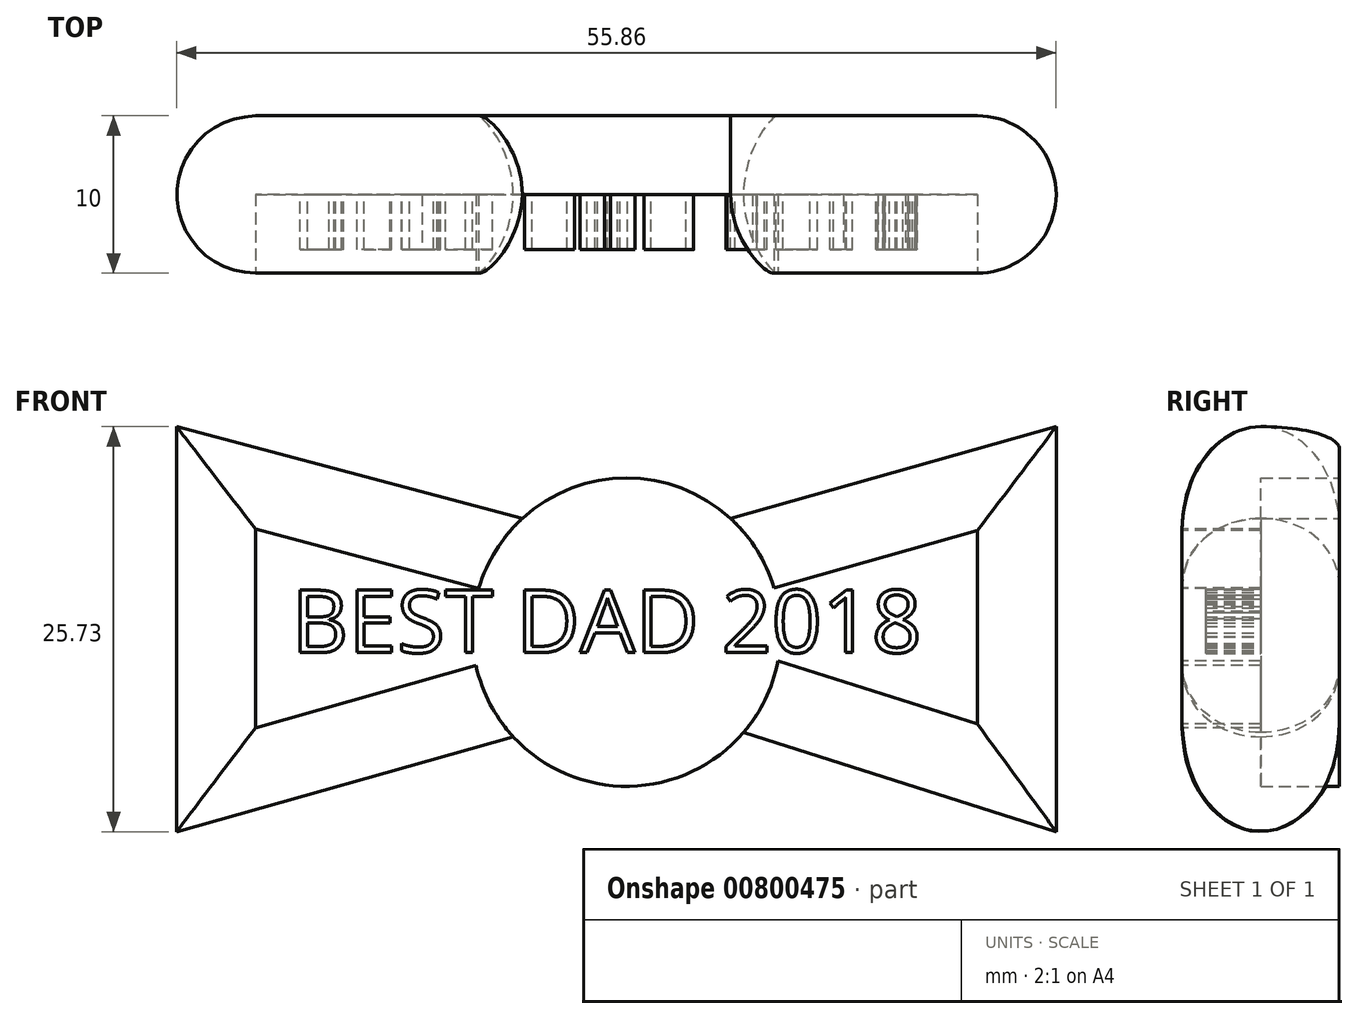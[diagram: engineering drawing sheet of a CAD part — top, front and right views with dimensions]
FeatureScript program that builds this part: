
annotation { "Feature Type Name" : "Feature", "Feature Type Description" : "" }
export const myFeature = defineFeature(function(context is Context, id is Id, definition is map)
    precondition{}
    {
        {
            var Q0;
            Q0=qCreatedBy(makeId("Front.planeOp"),FACE);
            var sketch = newSketch(context, id + "F0", { "sketchPlane" : qUnion([Q0])});
            skCircle(sketch, "E0", {"center": v(0, 0) * mm, "radius": 9.8 * mm});
            skLineSegment(sketch, "E1", {"start": v(6.62, 7.22) * mm, "end": v(27.3, 13.05) * mm});
            skLineSegment(sketch, "E2", {"start": v(27.3, 13.05) * mm, "end": v(27.3, -12.68) * mm});
            skLineSegment(sketch, "E3", {"start": v(27.3, -12.68) * mm, "end": v(7.43, -6.37) * mm});
            skLineSegment(sketch, "E4", {"start": v(7.43, -6.37) * mm, "end": v(6.62, 7.22) * mm});
            skLineSegment(sketch, "E5", {"start": v(-6.62, 7.22) * mm, "end": v(-28.57, 13.05) * mm});
            skLineSegment(sketch, "E6", {"start": v(-28.57, 13.05) * mm, "end": v(-28.57, -12.68) * mm});
            skLineSegment(sketch, "E7", {"start": v(-28.57, -12.68) * mm, "end": v(-7.2, -6.64) * mm});
            skLineSegment(sketch, "E8", {"start": v(-7.2, -6.64) * mm, "end": v(-6.62, 7.22) * mm});
            skSolve(sketch);
        }
        {
            var Q0;
            Q0 = qSketchRegion(id + "F0", true);
            extrude(context, id + "F1", {"entities" : qUnion([Q0]), "depth" : 10 * mm, "offsetDistance" : 25 * mm});
        }
        {
            var Q0;
            Q0=qCreatedBy(makeId("Front.planeOp"),FACE);
            var sketch = newSketch(context, id + "F2", { "sketchPlane" : qUnion([Q0])});
            skText(sketch, "E9", { "text": "BEST DAD 2018", "fontName": "OpenSans-Regular.ttf"});
            const initialGuessF2  = {"E9": [-0.02127, -0.0013, 1, 0, 0.004]};
            skSetInitialGuess(sketch, initialGuessF2);
            skSolve(sketch);
        }
        {
            var Q0;
            Q0=makeQuery(id+"F1.opExtrude","CAP_EDGE",EDGE,{"disambiguationData":[OSD([sQuery(id+"F0.wireOp",EDGE,"E5")])],"isStart":false});
            var Q1;
            Q1=makeQuery(id+"F1.opExtrude","CAP_EDGE",EDGE,{"disambiguationData":[OSD([sQuery(id+"F0.wireOp",EDGE,"E6")])],"isStart":false});
            var Q2;
            Q2=makeQuery(id+"F1.opExtrude","CAP_EDGE",EDGE,{"disambiguationData":[OSD([sQuery(id+"F0.wireOp",EDGE,"E7")])],"isStart":false});
            var Q3;
            Q3=makeQuery(id+"F1.opExtrude","CAP_EDGE",EDGE,{"disambiguationData":[OSD([sQuery(id+"F0.wireOp",EDGE,"E3")])],"isStart":false});
            var Q4;
            Q4=makeQuery(id+"F1.opExtrude","CAP_EDGE",EDGE,{"disambiguationData":[OSD([sQuery(id+"F0.wireOp",EDGE,"E2")])],"isStart":false});
            var Q5;
            Q5=makeQuery(id+"F1.opExtrude","CAP_EDGE",EDGE,{"disambiguationData":[OSD([sQuery(id+"F0.wireOp",EDGE,"E1")])],"isStart":false});
            var Q6;
            Q6=makeQuery(id+"F1.opExtrude","CAP_EDGE",EDGE,{"disambiguationData":[OSD([sQuery(id+"F0.wireOp",EDGE,"E5")])],"isStart":true});
            var Q7;
            Q7=makeQuery(id+"F1.opExtrude","CAP_EDGE",EDGE,{"disambiguationData":[OSD([sQuery(id+"F0.wireOp",EDGE,"E6")])],"isStart":true});
            var Q8;
            Q8=makeQuery(id+"F1.opExtrude","CAP_EDGE",EDGE,{"disambiguationData":[OSD([sQuery(id+"F0.wireOp",EDGE,"E7")])],"isStart":true});
            var Q9;
            Q9=makeQuery(id+"F1.opExtrude","CAP_EDGE",EDGE,{"disambiguationData":[OSD([sQuery(id+"F0.wireOp",EDGE,"E3")])],"isStart":true});
            var Q10;
            Q10=makeQuery(id+"F1.opExtrude","CAP_EDGE",EDGE,{"disambiguationData":[OSD([sQuery(id+"F0.wireOp",EDGE,"E2")])],"isStart":true});
            fillet(context, id + "F3", {"entities" : qUnion([Q0, Q1, Q2, Q3, Q4, Q5, Q6, Q7, Q8, Q9, Q10]), "tangentPropagation" : true, "radius" : 5 * mm, "defaultsChanged" : false, "vertexSettings" : [], "allowEdgeOverflow" : false});
        }
        {
            var Q0;
            Q0=makeQuery(id+"F1.opExtrude","CAP_FACE",FACE,{"disambiguationData":[OSD([sQuery(id+"F0.wireOp",EDGE,"E0"),sQuery(id+"F0.wireOp",EDGE,"E1"),sQuery(id+"F0.wireOp",EDGE,"E2"),sQuery(id+"F0.wireOp",EDGE,"E3"),sQuery(id+"F0.wireOp",EDGE,"E5"),sQuery(id+"F0.wireOp",EDGE,"E6"),sQuery(id+"F0.wireOp",EDGE,"E7")])],"isStart":false});
            extrude(context, id + "F4", {"entities" : qUnion([Q0]), "operationType" : NewBodyOperationType.REMOVE, "oppositeDirection" : true, "depth" : 5 * mm, "offsetDistance" : 25 * mm});
        }
        {
            var Q0;
            Q0 = qSketchRegion(id + "F2", true);
            extrude(context, id + "F5", {"entities" : qUnion([Q0]), "operationType" : NewBodyOperationType.ADD, "depth" : 8.5 * mm, "offsetDistance" : 25 * mm});
        }
    });
